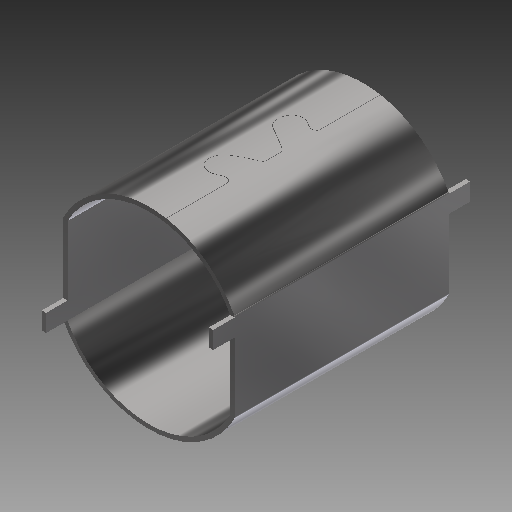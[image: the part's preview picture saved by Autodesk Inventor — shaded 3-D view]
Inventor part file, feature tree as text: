
AUTODESK INVENTOR PART (.ipt)
format: ipt  version: 2019 (Build 230136000, 136)  size: 288,768 bytes
history: native  units: mm
features: sketch x3, extrude x2, plane x1, mirror x1, projected_geometry x1, other x1
ambient origin geometry x8: Origin, YZ Plane, XZ Plane, XY Plane, X Axis, Y Axis, Z Axis, Center Point
bodies: Solid1 (feature_tree)
feature tree (9):
  extrude  "Extrusion1"  Depth=40.0mm
  plane  "Work Plane1"
  extrude  "Extrusion2"  Depth=22.5mm
  mirror  "Mirror1"
  sketch  "Sketch1"  dims[d0=35.0mm d1=40.0mm]
  sketch  "Sketch2"  dims[d2=20.0mm d3=22.5mm]
  projected_geometry  "Projected Loop1"
  sketch  "Sketch3"  dims[d4=1.0mm d5=50.0mm d6=0.0mm d8=60.0deg d9=6.0mm d11=4.0mm d12=1.0mm d13=1.0mm d14=0.1mm d15=3.0mm d16=0.0mm d17=0.005mm d19=1.005mm d20=22.5mm d21=14.113249mm d22=22.5mm d23=6.0mm d24=6.0mm d25=5.0mm d26=0.0mm d27=1.0mm]
  other  "Cut1"
